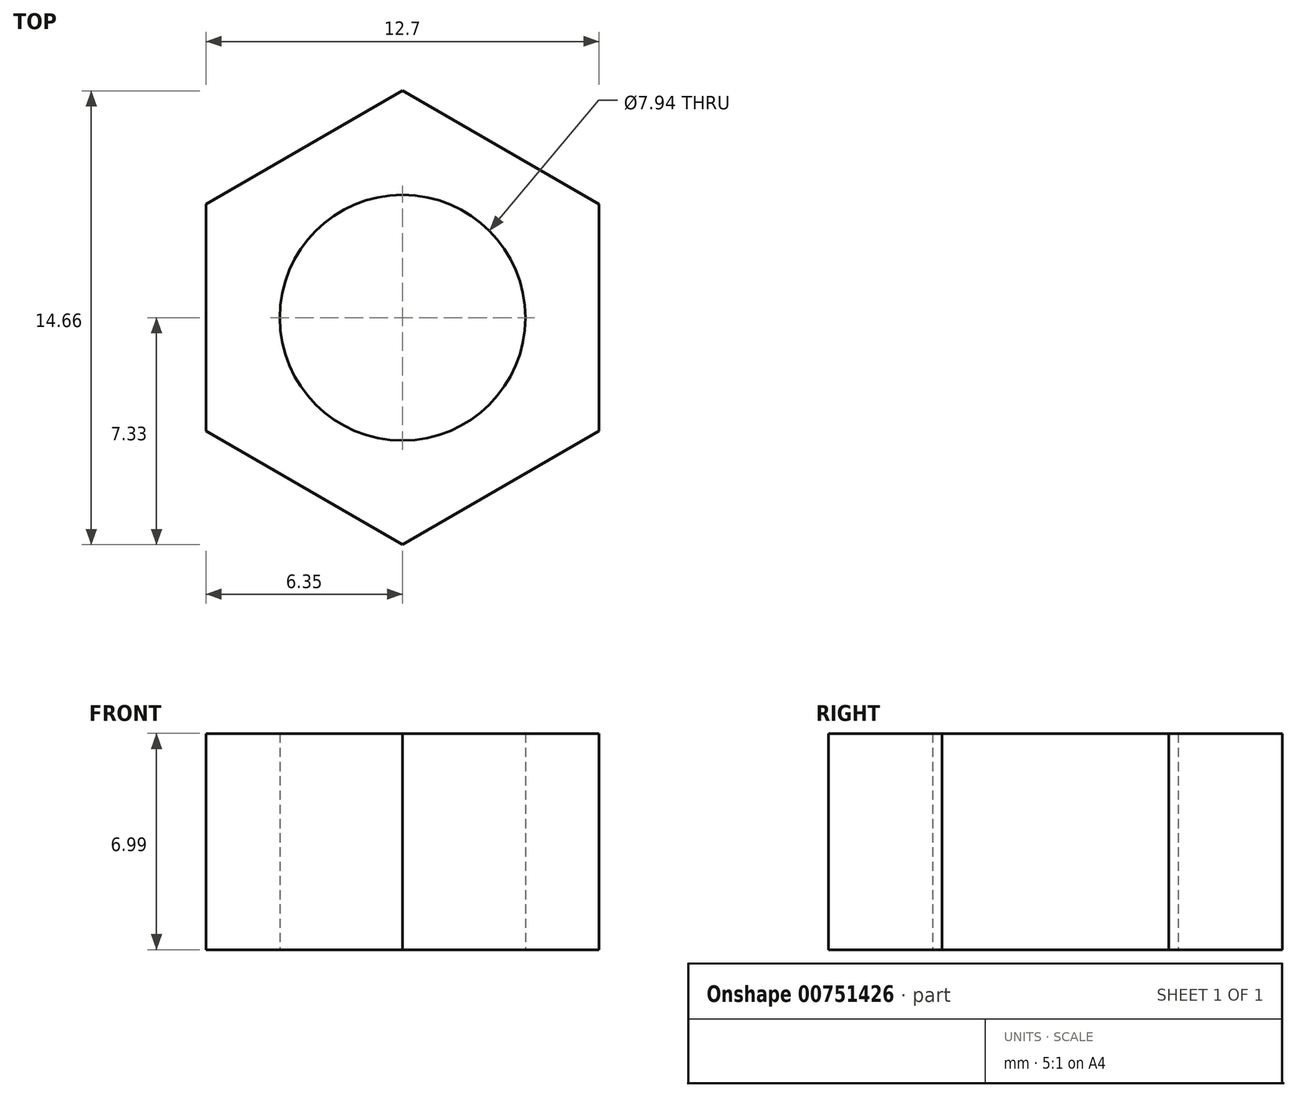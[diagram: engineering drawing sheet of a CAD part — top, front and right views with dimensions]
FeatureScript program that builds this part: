
annotation { "Feature Type Name" : "Feature", "Feature Type Description" : "" }
export const myFeature = defineFeature(function(context is Context, id is Id, definition is map)
    precondition{}
    {
        {
            var Q0;
            Q0=qCreatedBy(makeId("Top.planeOp"),FACE);
            var sketch = newSketch(context, id + "F0", { "sketchPlane" : qUnion([Q0])});
            skCircle(sketch, "E0.cCircle", {"center": v(0, 0) * mm, "radius": 6.35 * mm, "construction": true});
            skLineSegment(sketch, "E0.0", {"start": v(6.35, 3.67) * mm, "end": v(6.35, -3.67) * mm});
            skLineSegment(sketch, "E0.1", {"start": v(6.35, -3.67) * mm, "end": v(0, -7.33) * mm});
            skLineSegment(sketch, "E0.2", {"start": v(0, -7.33) * mm, "end": v(-6.35, -3.67) * mm});
            skLineSegment(sketch, "E0.3", {"start": v(-6.35, -3.67) * mm, "end": v(-6.35, 3.67) * mm});
            skLineSegment(sketch, "E0.4", {"start": v(-6.35, 3.67) * mm, "end": v(0, 7.33) * mm});
            skLineSegment(sketch, "E0.5", {"start": v(0, 7.33) * mm, "end": v(6.35, 3.67) * mm});
            skPoint(sketch, "E0.0.midPoint", {"position": v(6.35, 0) * mm});
            skCircle(sketch, "E1", {"center": v(0, 0) * mm, "radius": 3.97 * mm});
            skSolve(sketch);
        }
        {
            var Q0;
            Q0=makeQuery(id+"F0.imprint","IMPRINT",FACE,{"disambiguationData":[TD([[makeQuery(id+"F0.imprint","IMPRINT",EDGE,{"derivedFrom":sQuery(id+"F0.wireOp",EDGE,"E0.0")}),-1.0]])]});
            extrude(context, id + "F1", {"entities" : qUnion([Q0]), "depth" : 7 * mm, "offsetDistance" : 25.4 * mm});
        }
    });
